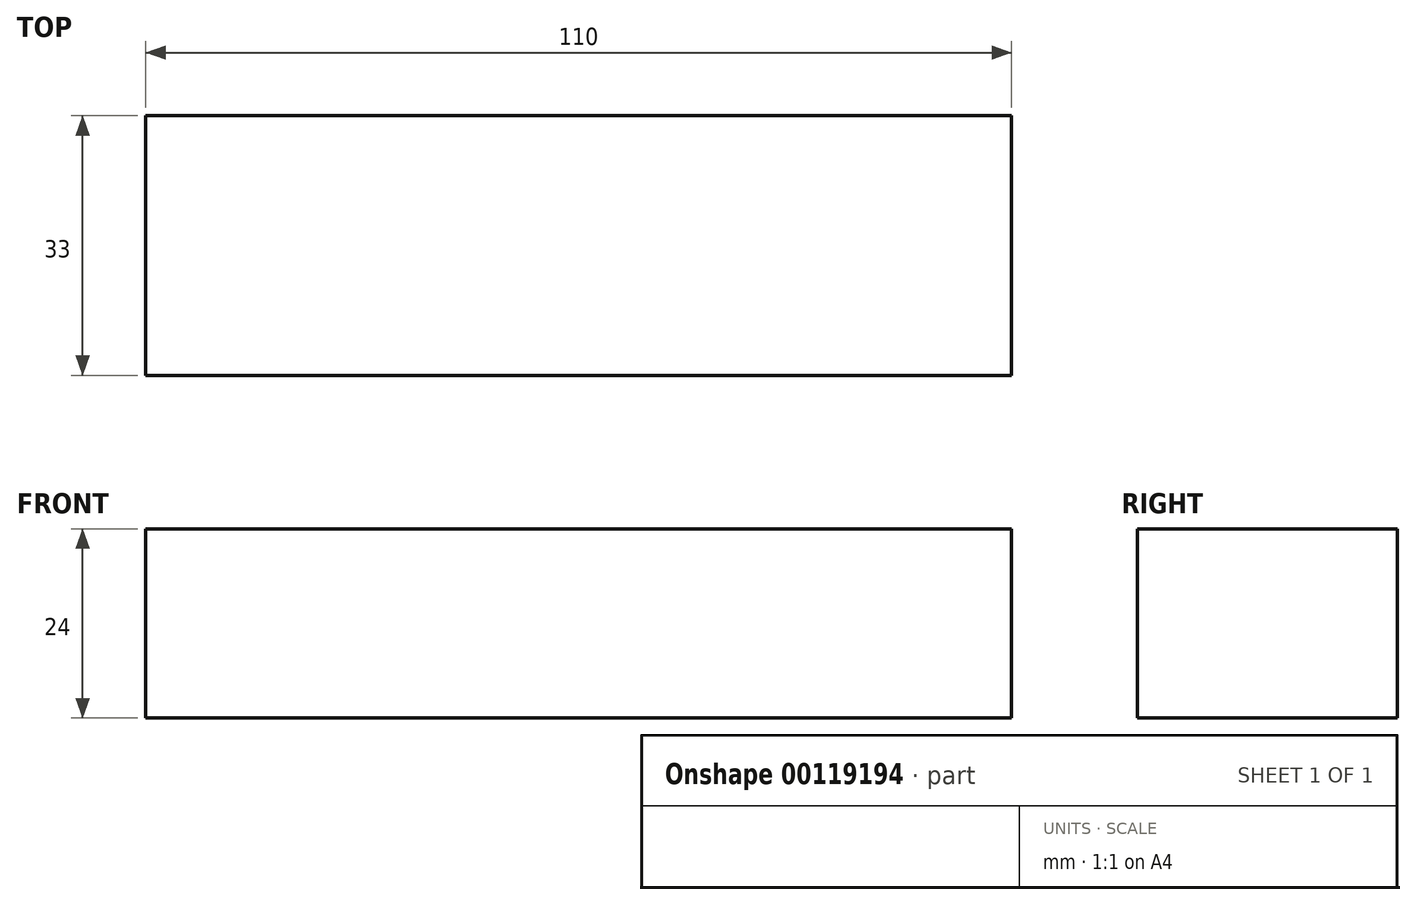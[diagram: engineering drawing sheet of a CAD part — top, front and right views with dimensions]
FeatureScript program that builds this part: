
annotation { "Feature Type Name" : "Feature", "Feature Type Description" : "" }
export const myFeature = defineFeature(function(context is Context, id is Id, definition is map)
    precondition{}
    {
        {
            var Q0;
            Q0=qCreatedBy(makeId("Top.planeOp"),FACE);
            var sketch = newSketch(context, id + "F0", { "sketchPlane" : qUnion([Q0])});
            skLineSegment(sketch, "E0.bottom", {"start": v(55, -16.5) * mm, "end": v(-55, -16.5) * mm});
            skLineSegment(sketch, "E0.top", {"start": v(55, 16.5) * mm, "end": v(-55, 16.5) * mm});
            skLineSegment(sketch, "E0.left", {"start": v(55, -16.5) * mm, "end": v(55, 16.5) * mm});
            skLineSegment(sketch, "E0.right", {"start": v(-55, -16.5) * mm, "end": v(-55, 16.5) * mm});
            skPoint(sketch, "E0.middle", {"position": v(0, 0) * mm});
            skSolve(sketch);
        }
        {
            var Q0;
            Q0=makeQuery(id+"F0.imprint","IMPRINT",FACE,{"disambiguationData":[TD([[makeQuery(id+"F0.imprint","IMPRINT",EDGE,{"derivedFrom":sQuery(id+"F0.wireOp",EDGE,"E0.bottom")}),-1.0]])]});
            extrude(context, id + "F1", {"entities" : qUnion([Q0]), "depth" : 24 * mm});
        }
        {
            var Q0;
            Q0=qCreatedBy(makeId("Top.planeOp"),FACE);
            var sketch = newSketch(context, id + "F2", { "sketchPlane" : qUnion([Q0])});
            skLineSegment(sketch, "E1.bottom", {"start": v(10, -7.5) * mm, "end": v(-10, -7.5) * mm});
            skLineSegment(sketch, "E1.top", {"start": v(10, 7.5) * mm, "end": v(-10, 7.5) * mm});
            skLineSegment(sketch, "E1.left", {"start": v(10, -7.5) * mm, "end": v(10, 7.5) * mm});
            skLineSegment(sketch, "E1.right", {"start": v(-10, -7.5) * mm, "end": v(-10, 7.5) * mm});
            skPoint(sketch, "E1.middle", {"position": v(0, 0) * mm});
            skCircle(sketch, "E2", {"center": v(-7.5, 5) * mm, "radius": 1.5 * mm});
            skCircle(sketch, "E3", {"center": v(7.5, 5) * mm, "radius": 1.5 * mm});
            skLineSegment(sketch, "E4.bottom", {"start": v(1.95, -1.95) * mm, "end": v(-1.95, -1.95) * mm});
            skLineSegment(sketch, "E4.top", {"start": v(1.95, 1.95) * mm, "end": v(-1.95, 1.95) * mm});
            skLineSegment(sketch, "E4.left", {"start": v(1.95, -1.95) * mm, "end": v(1.95, 1.95) * mm});
            skLineSegment(sketch, "E4.right", {"start": v(-1.95, -1.95) * mm, "end": v(-1.95, 1.95) * mm});
            skSolve(sketch);
        }
        {
            var Q0;
            Q0=makeQuery(id+"F2.imprint","IMPRINT",FACE,{"disambiguationData":[TD([[makeQuery(id+"F2.imprint","IMPRINT",EDGE,{"derivedFrom":sQuery(id+"F2.wireOp",EDGE,"E1.bottom")}),-1.0]])]});
            extrude(context, id + "F3", {"entities" : qUnion([Q0]), "depth" : 1.5 * mm});
        }
        {
            var Q0;
            Q0=makeQuery(id+"F2.imprint","IMPRINT",FACE,{"disambiguationData":[TD([[makeQuery(id+"F2.imprint","IMPRINT",EDGE,{"derivedFrom":sQuery(id+"F2.wireOp",EDGE,"E4.bottom")}),-1.0]])]});
            extrude(context, id + "F4", {"entities" : qUnion([Q0]), "operationType" : NewBodyOperationType.ADD, "depth" : 2.35 * mm});
        }
    });
